# Revit family: EN MRT 2660
name_source: partatom
category: Equipement spécialisé
units: mm (PartAtom-declared; Revit-internal decimal feet)

## family parameters
Basée sur le plan de construction = Non
Cote de connecteur circulaire = Utiliser le diamètre
Couper avec des vides une fois chargée = Non
Numéro OmniClass = 23.50.30.00
Partagée = Non
Point de calcul de pièce = Non
Titre OmniClass = Materials Handling
Toujours verticalement = Oui
Type d'élément = Normal

## types (1)
- MRT 2660
    Average consumption (L/h) = 8.31
    CO2 emissions = 21.85
    Commentaires du type = Chariot télescopique rotatif tout terrain
    Créé par = ATLANCAD
    Elévation par défaut = 0.00 m
    Engine norm = Stage V / Tier 4
    External turning radius over tyres = 4.22 m
    Fabricant = MANITOU
    Ground clearance = 0.36 m
    I.C. Engine power rating - Power (ch) = 156
    I.C. Engine power rating - Power (kW) = 115
    Max. capacity = 6000.00 kg
    Max. lifting height = 25.90 m
    Max. outreach = 21.70 m
    Modèle = MRT 2145
    Noise at driving position (LpA) in dB(A) = 0
    Noise to environment (LwA) = 0
    Overall cab width = 8.08 m
    Overall height = 3.10 m
    Overall width = 2.50 m
    Tilt-down angle = 112.00°
    Tilt-up angle = 12.00°
    URL = www.manitou.com
    Weight = 18000.00 kg
    Wheelbase = 3.05 m
